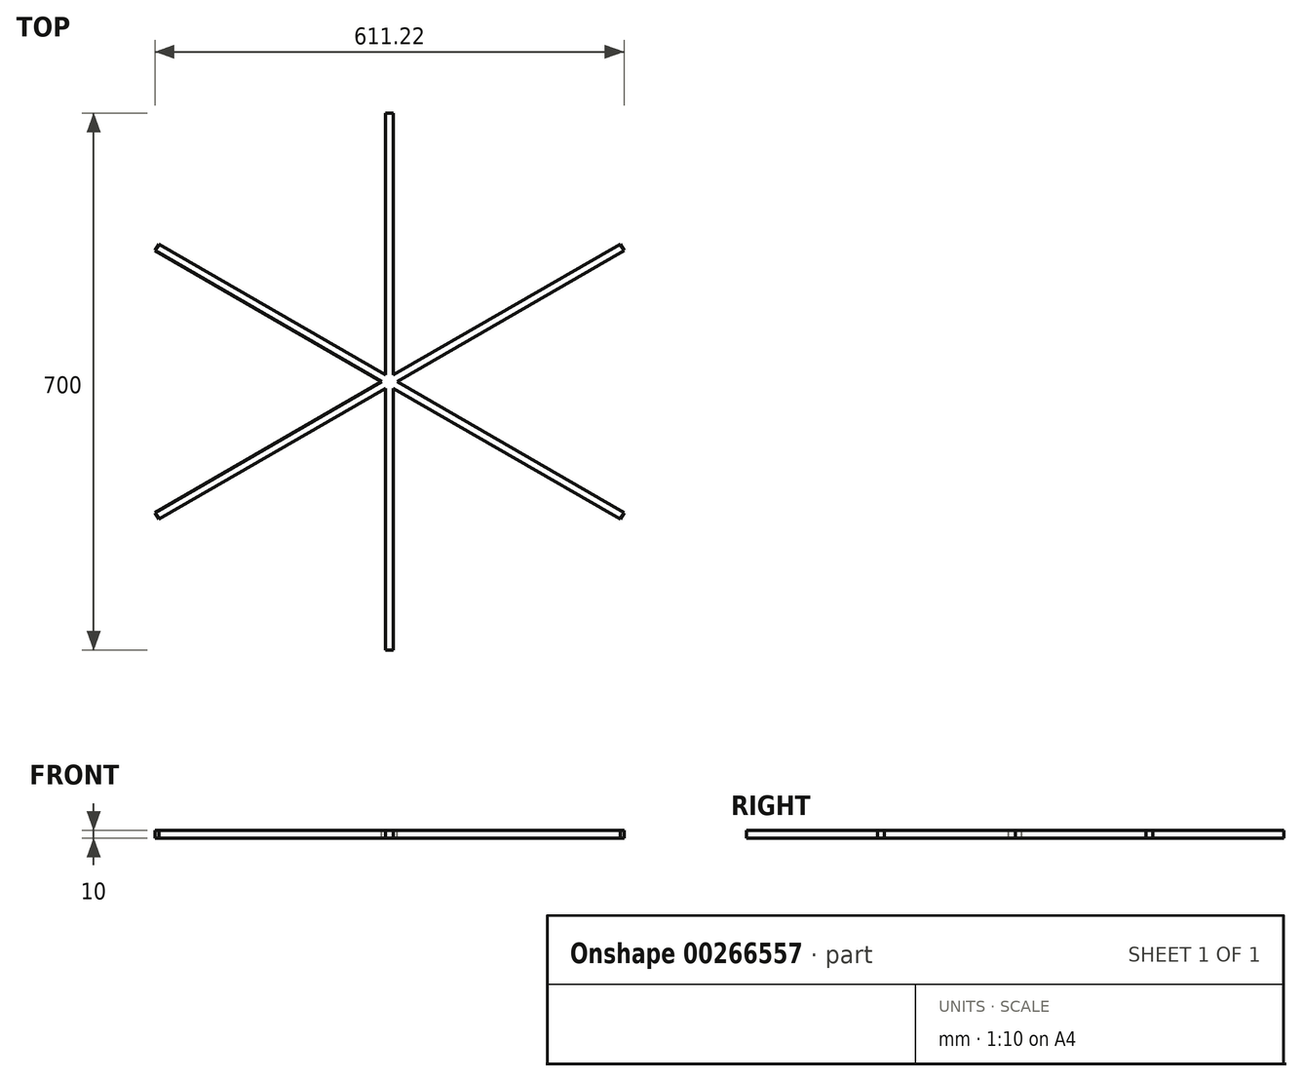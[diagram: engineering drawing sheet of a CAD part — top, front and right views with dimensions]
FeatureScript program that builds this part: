
annotation { "Feature Type Name" : "Feature", "Feature Type Description" : "" }
export const myFeature = defineFeature(function(context is Context, id is Id, definition is map)
    precondition{}
    {
        {
            var Q0;
            Q0=qCreatedBy(makeId("Top.planeOp"),FACE);
            var sketch = newSketch(context, id + "F0", { "sketchPlane" : qUnion([Q0])});
            skLineSegment(sketch, "E0", {"start": v(0, 0) * mm, "end": v(5, 0) * mm});
            skLineSegment(sketch, "E1", {"start": v(5, 0) * mm, "end": v(5, 350) * mm});
            skLineSegment(sketch, "E2", {"start": v(5, 350) * mm, "end": v(0, 350) * mm});
            skLineSegment(sketch, "E3.MirrorCS", {"start": v(-5, 0) * mm, "end": v(-5, 350) * mm});
            skLineSegment(sketch, "E4.MirrorCS", {"start": v(0, 0) * mm, "end": v(-5, 0) * mm});
            skLineSegment(sketch, "E5.MirrorCS", {"start": v(-5, 350) * mm, "end": v(0, 350) * mm});
            skSolve(sketch);
        }
        {
            var Q0;
            Q0 = qSketchRegion(id + "F0", true);
            extrude(context, id + "F1", {"entities" : qUnion([Q0]), "depth" : 10 * mm});
        }
        {
            var Q0;
            Q0=makeQuery(id+"F1.opExtrude","SWEPT_FACE",FACE,{"disambiguationData":[OSD([sQuery(id+"F0.wireOp",EDGE,"E0"),sQuery(id+"F0.wireOp",EDGE,"E4.MirrorCS")])]});
            var sketch = newSketch(context, id + "F2", { "sketchPlane" : qUnion([Q0])});
            skLineSegment(sketch, "E6", {"start": v(0, 0) * mm, "end": v(0, 10) * mm, "construction": true});
            skSolve(sketch);
        }
        {
            var Q0;
            Q0=makeQuery(id+"F1.opExtrude","SWEPT_BODY",BODY,{"disambiguationData":[OSD([sQuery(id+"F0.wireOp",EDGE,"E0"),sQuery(id+"F0.wireOp",EDGE,"E1"),sQuery(id+"F0.wireOp",EDGE,"E2"),sQuery(id+"F0.wireOp",EDGE,"E3.MirrorCS"),sQuery(id+"F0.wireOp",EDGE,"E4.MirrorCS"),sQuery(id+"F0.wireOp",EDGE,"E5.MirrorCS")])]});
            var Q1;
            Q1=sQuery(id+"F2.wireOp",EDGE,"E6");
            circularPattern(context, id + "F3", {"operationType" : NewBodyOperationType.ADD, "entities" : qUnion([Q0]), "axis" : qUnion([Q1]), "angle" : 360 * degree, "instanceCount" : 6, "equalSpace" : true});
        }
    });
